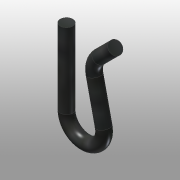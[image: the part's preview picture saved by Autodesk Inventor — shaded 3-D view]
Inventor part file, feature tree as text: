
AUTODESK INVENTOR PART (.ipt)
format: ipt  version: 2015 (Build 190159000, 159)  size: 117,248 bytes
history: native  units: mm
features: other x3, sketch x2
ambient origin geometry x8: Origin, YZ Plane, XZ Plane, XY Plane, X Axis, Y Axis, Z Axis, Center Point
bodies: Solid1 (feature_tree)
feature tree (5):
  other  "500-177.ipt"
  other  "Solid1::500-177.ipt"
  other  "TaggingFeature1"
  sketch  "Sketch1"  dims[d0=10.0mm]
  sketch  "Sketch2"
